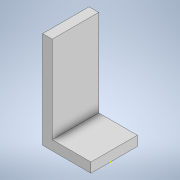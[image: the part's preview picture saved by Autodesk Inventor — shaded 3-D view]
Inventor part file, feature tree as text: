
AUTODESK INVENTOR PART (.ipt)
format: ipt  version: 2021 (Build 250183000, 183)  size: 114,688 bytes
history: native  units: mm
features: sketch x4, extrude x3
ambient origin geometry x8: Origin, YZ Plane, XZ Plane, XY Plane, X Axis, Y Axis, Z Axis, Center Point
bodies: Solid1 (feature_tree)
feature tree (7):
  extrude  "Extrusion1"  Depth=25.0mm
  extrude  "Extrusion2"  Depth=5.0mm
  sketch  "Sketch3"  dims[d5=45.0mm d6=0.0mm d7=14.0mm d8=0.0mm]
  extrude  "Extrusion3"  Depth=45.0mm TaperAngle=0.0deg
  sketch  "Sketch1"  dims[d0=25.0mm d1=10.0mm]
  sketch  "Sketch2"  dims[d2=5.0mm d3=0.0mm d4=5.0mm]
  sketch  "Sketch4"
